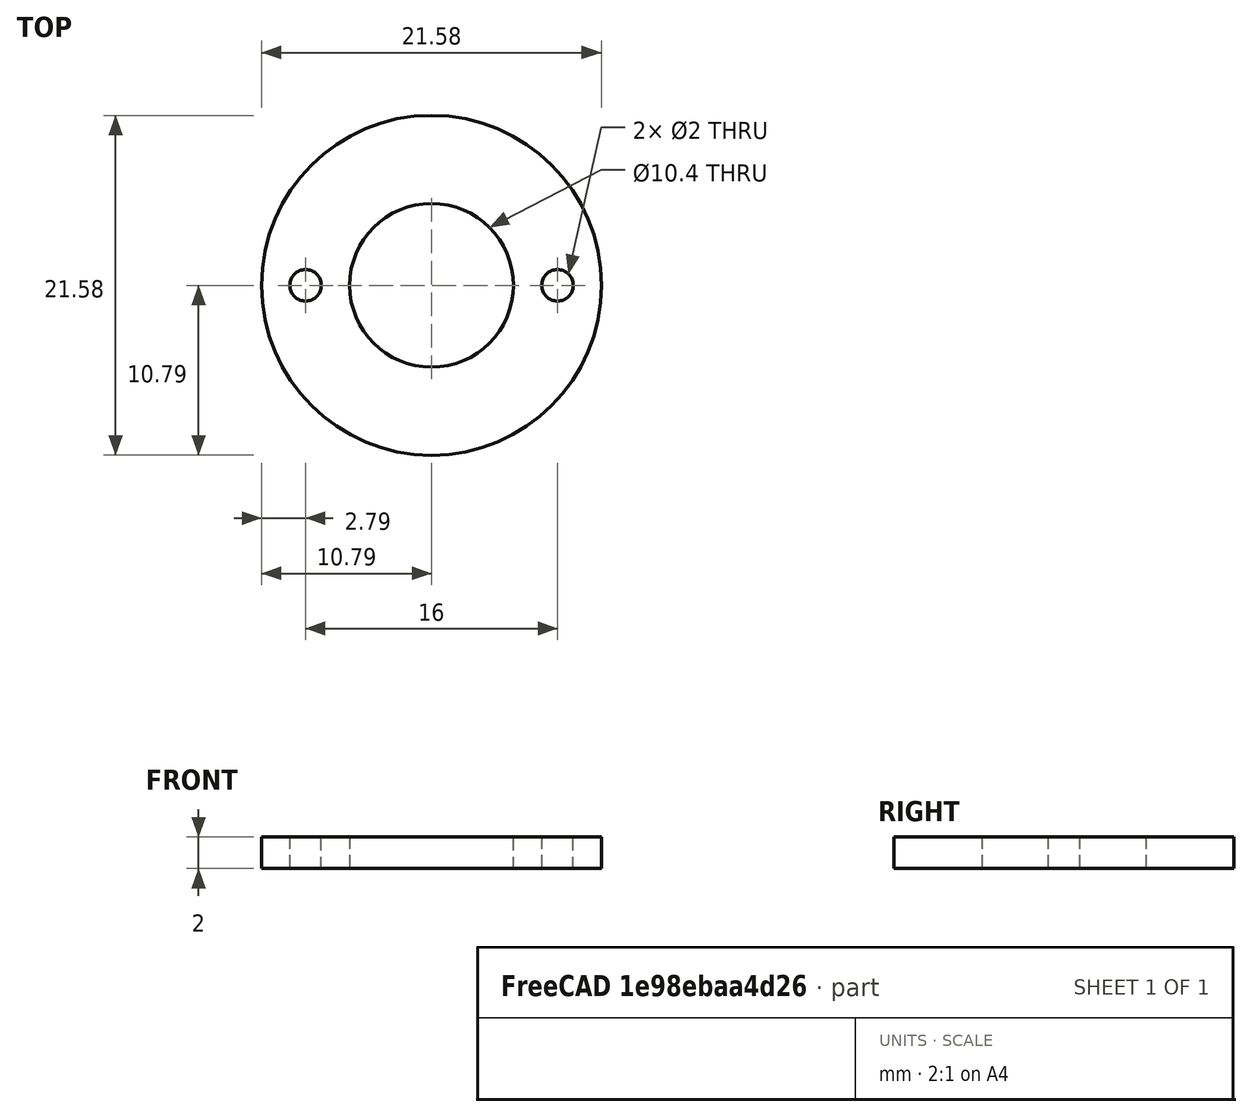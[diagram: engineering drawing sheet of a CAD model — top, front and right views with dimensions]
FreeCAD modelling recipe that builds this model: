
FCSTD DOCUMENT  (FreeCAD 1.0R39109 (Git))
Label: windowVerticalBlindControl
License: All rights reserved
LicenseURL: http://en.wikipedia.org/wiki/All_rights_reserved
objects: Sketcher::SketchObject×1, Spreadsheet::Sheet×1, PartDesign::Pad×1, PartDesign::Body×1
note: 6 computed .brp shape members not serialized (recipe doc carries the construction recipe); baked Part::Feature solids carry a one-line shape summary decoded from their .brp

FEATURE [Sketcher::SketchObject] Sketch
  ArcFitTolerance = 0
  AttachmentSupport = -> [XY_Plane]
  FullyConstrained = false
  MakeInternals = false
  MapMode = 5
  expr: Constraints[4] = Spreadsheet.motorCenterPopupR
  expr: Constraints[5] = Spreadsheet.motorScrewR
  expr: Constraints[6] = Spreadsheet.motorScrewR
  expr: Constraints[7] = Spreadsheet.motoScrewHoleR
  expr: Constraints[8] = Spreadsheet.motoScrewHoleR
  sketch-geometry (4):
    g0: Circle CenterX=0 CenterY=0 CenterZ=0 NormalX=0 NormalY=0 NormalZ=1 AngleXU=0 Radius=10.7942
    g1: Circle CenterX=8 CenterY=0 CenterZ=0 NormalX=0 NormalY=0 NormalZ=1 AngleXU=0 Radius=1
    g2: Circle CenterX=-8 CenterY=0 CenterZ=0 NormalX=0 NormalY=0 NormalZ=1 AngleXU=0 Radius=1
    g3: Circle CenterX=0 CenterY=0 CenterZ=0 NormalX=0 NormalY=0 NormalZ=1 AngleXU=0 Radius=5.2
  constraints (9):
    c: Coincident(g0,g-1)
    c: PointOnObject(g1,g-1)
    c: PointOnObject(g2,g-1)
    c: Coincident(g3,g0)
    c: Radius(g3) = 5.2
    c: DistanceX(g0,g1) = 8
    c: DistanceX(g2,g0) = 8
    c: Radius(g1) = 1
    c: Radius(g2) = 1
FEATURE [Spreadsheet::Sheet] Spreadsheet
  cells = A2='shaftR; B2(shaftR)==2.3 / 2; A3='motorScrewR; B3(motorScrewR)=8; A4='motorScrewHoleR; B4(motoScrewHoleR)=1; A5='motorCenterPopupR; B5(motorCenterPopupR)=5.2
FEATURE [PartDesign::Pad] Pad
  Direction = (0,0,1)
  Length = 2
  Length2 = 10
  Profile = -> Sketch
  ReferenceAxis = -> Sketch [N_Axis]
  Suppressed = false
  Type = 0
FEATURE [PartDesign::Body] Body
  AllowCompound = false
  Group = -> [Sketch,Pad]
  Origin = -> Origin
  Tip = -> Pad
